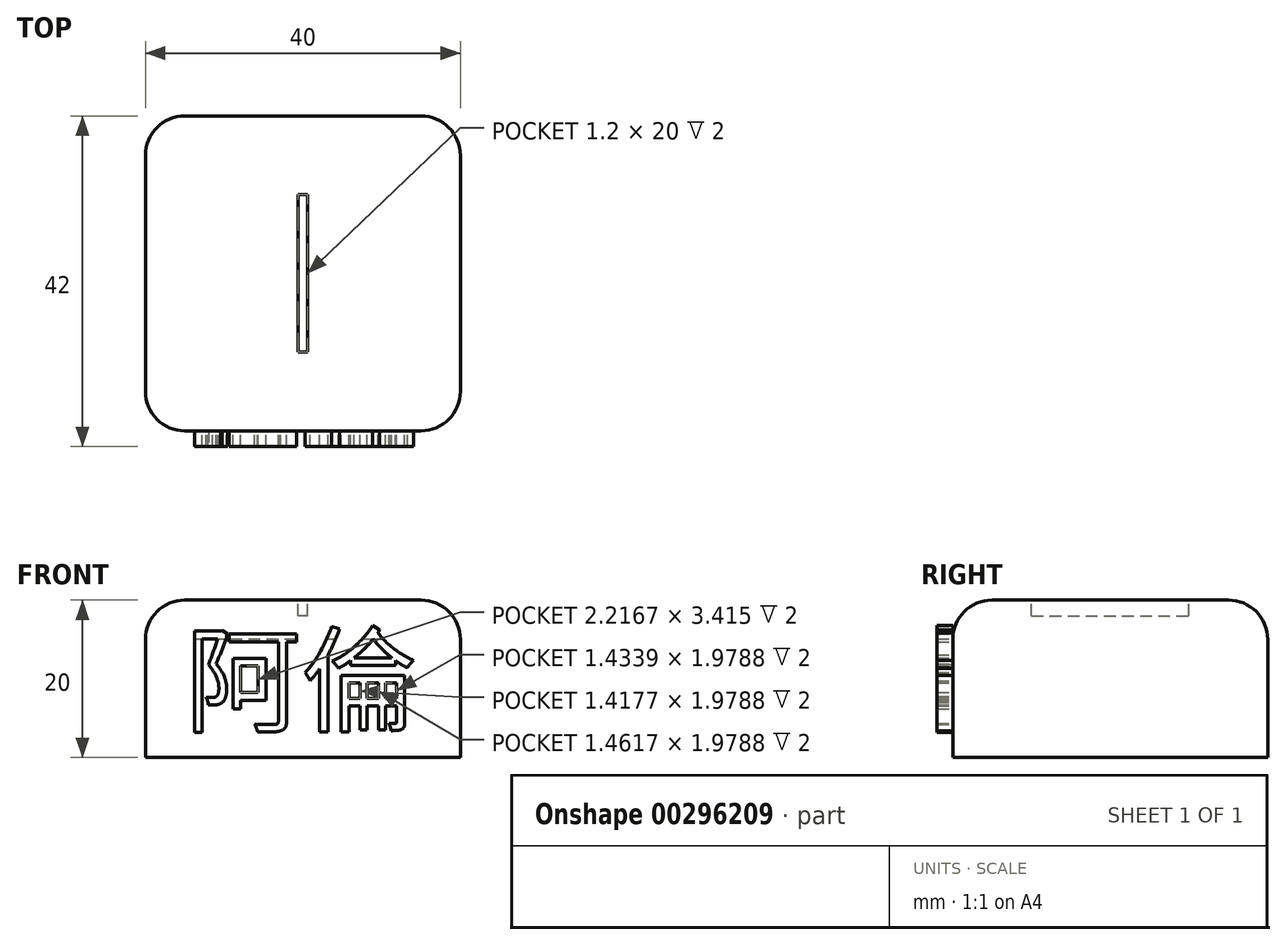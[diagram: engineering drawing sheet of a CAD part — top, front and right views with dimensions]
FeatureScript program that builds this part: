
annotation { "Feature Type Name" : "Feature", "Feature Type Description" : "" }
export const myFeature = defineFeature(function(context is Context, id is Id, definition is map)
    precondition{}
    {
        {
            var Q0;
            Q0=qCreatedBy(makeId("Top.planeOp"),FACE);
            var sketch = newSketch(context, id + "F0", { "sketchPlane" : qUnion([Q0])});
            skLineSegment(sketch, "E0.bottom", {"start": v(20, -20) * mm, "end": v(-20, -20) * mm});
            skLineSegment(sketch, "E0.top", {"start": v(20, 20) * mm, "end": v(-20, 20) * mm});
            skLineSegment(sketch, "E0.left", {"start": v(20, -20) * mm, "end": v(20, 20) * mm});
            skLineSegment(sketch, "E0.right", {"start": v(-20, -20) * mm, "end": v(-20, 20) * mm});
            skPoint(sketch, "E0.middle", {"position": v(0, 0) * mm});
            skLineSegment(sketch, "E1.bottom", {"start": v(0.6, -10) * mm, "end": v(-0.6, -10) * mm});
            skLineSegment(sketch, "E1.top", {"start": v(0.6, 10) * mm, "end": v(-0.6, 10) * mm});
            skLineSegment(sketch, "E1.left", {"start": v(0.6, -10) * mm, "end": v(0.6, 10) * mm});
            skLineSegment(sketch, "E1.right", {"start": v(-0.6, -10) * mm, "end": v(-0.6, 10) * mm});
            skSolve(sketch);
        }
        {
            var Q0;
            Q0=makeQuery(id+"F0.imprint","IMPRINT",FACE,{"disambiguationData":[TD([[makeQuery(id+"F0.imprint","IMPRINT",EDGE,{"derivedFrom":sQuery(id+"F0.wireOp",EDGE,"E0.bottom")}),-1.0]])]});
            var Q1;
            Q1=makeQuery(id+"F0.imprint","IMPRINT",FACE,{"disambiguationData":[TD([[makeQuery(id+"F0.imprint","IMPRINT",EDGE,{"derivedFrom":sQuery(id+"F0.wireOp",EDGE,"E1.bottom")}),-1.0]])]});
            extrude(context, id + "F1", {"entities" : qUnion([Q0, Q1]), "oppositeDirection" : true, "depth" : 20 * mm});
        }
        {
            var Q0;
            Q0=makeQuery(id+"F0.imprint","IMPRINT",FACE,{"disambiguationData":[TD([[makeQuery(id+"F0.imprint","IMPRINT",EDGE,{"derivedFrom":sQuery(id+"F0.wireOp",EDGE,"E1.bottom")}),-1.0]])]});
            extrude(context, id + "F2", {"entities" : qUnion([Q0]), "operationType" : NewBodyOperationType.REMOVE, "oppositeDirection" : true, "depth" : 2 * mm});
        }
        {
            var Q0;
            Q0=makeQuery(id+"F2.boolean.opBoolean","COPY",EDGE,{"derivedFrom":makeQuery(id+"F2.opExtrude","CAP_EDGE",EDGE,{"disambiguationData":[OSD([sQuery(id+"F0.wireOp",EDGE,"E1.left")])],"isStart":true})});
            var Q1;
            Q1=makeQuery(id+"F2.boolean.opBoolean","COPY",EDGE,{"derivedFrom":makeQuery(id+"F2.opExtrude","CAP_EDGE",EDGE,{"disambiguationData":[OSD([sQuery(id+"F0.wireOp",EDGE,"E1.right")])],"isStart":true})});
            var Q2;
            Q2=makeQuery(id+"F1.opExtrude","SWEPT_EDGE",EDGE,{"disambiguationData":[OSD([sQuery(id+"F0.wireOp",EDGE,"E0.bottom"),sQuery(id+"F0.wireOp",EDGE,"E0.left")])]});
            var Q3;
            Q3=makeQuery(id+"F1.opExtrude","SWEPT_EDGE",EDGE,{"disambiguationData":[OSD([sQuery(id+"F0.wireOp",EDGE,"E0.top"),sQuery(id+"F0.wireOp",EDGE,"E0.left")])]});
            var Q4;
            Q4=makeQuery(id+"F1.opExtrude","CAP_EDGE",EDGE,{"disambiguationData":[OSD([sQuery(id+"F0.wireOp",EDGE,"E0.left")])],"isStart":true});
            var Q5;
            Q5=makeQuery(id+"F1.opExtrude","SWEPT_EDGE",EDGE,{"disambiguationData":[OSD([sQuery(id+"F0.wireOp",EDGE,"E0.bottom"),sQuery(id+"F0.wireOp",EDGE,"E0.right")])]});
            var Q6;
            Q6=makeQuery(id+"F1.opExtrude","SWEPT_EDGE",EDGE,{"disambiguationData":[OSD([sQuery(id+"F0.wireOp",EDGE,"E0.top"),sQuery(id+"F0.wireOp",EDGE,"E0.right")])]});
            var Q7;
            Q7=makeQuery(id+"F1.opExtrude","CAP_EDGE",EDGE,{"disambiguationData":[OSD([sQuery(id+"F0.wireOp",EDGE,"E0.top")])],"isStart":true});
            var Q8;
            Q8=makeQuery(id+"F1.opExtrude","CAP_EDGE",EDGE,{"disambiguationData":[OSD([sQuery(id+"F0.wireOp",EDGE,"E0.right")])],"isStart":true});
            var Q9;
            Q9=makeQuery(id+"F1.opExtrude","CAP_EDGE",EDGE,{"disambiguationData":[OSD([sQuery(id+"F0.wireOp",EDGE,"E0.bottom")])],"isStart":true});
            fillet(context, id + "F3", {"entities" : qUnion([Q0, Q1, Q2, Q3, Q4, Q5, Q6, Q7, Q8, Q9]), "radius" : 5 * mm, "tangentPropagation" : true, "allowEdgeOverflow" : false});
        }
        {
            var Q0;
            Q0=makeQuery(id+"F1.opExtrude","SWEPT_FACE",FACE,{"disambiguationData":[OSD([sQuery(id+"F0.wireOp",EDGE,"E0.bottom")])]});
            var sketch = newSketch(context, id + "F4", { "sketchPlane" : qUnion([Q0])});
            skText(sketch, "E2", { "text": "阿倫", "fontName": "NotoSansCJKtc-Regular.otf"});
            const initialGuessF4  = {"E2": [-0.015, -0.01564, 1, 0, 0.01064]};
            skSetInitialGuess(sketch, initialGuessF4);
            skSolve(sketch);
        }
        {
            var Q0;
            Q0=makeQuery(id+"F4.imprint","IMPRINT",FACE,{"disambiguationData":[TD([[makeQuery(id+"F4.imprint","IMPRINT",EDGE,{"derivedFrom":sQuery(id+"F4.wireOp",EDGE,"E2.sketch_text.stroke-18")}),1.0]])]});
            var Q1;
            Q1=makeQuery(id+"F4.imprint","IMPRINT",FACE,{"disambiguationData":[TD([[makeQuery(id+"F4.imprint","IMPRINT",EDGE,{"derivedFrom":sQuery(id+"F4.wireOp",EDGE,"E2.sketch_text.stroke-0")}),1.0]])]});
            var Q2;
            {var subQ1=sQuery(id+"F4.wireOp",EDGE,"E2.sketch_text.stroke-7");Q2=makeQuery(id+"F4.imprint","IMPRINT",FACE,{"disambiguationData":[TD([[makeQuery(id+"F4.imprint","IMPRINT",EDGE,{"derivedFrom":subQ1}),1.0]])]});}
            var Q3;
            {var subQ0=sQuery(id+"F4.wireOp",EDGE,"E2.sketch_text.stroke-3");Q3=makeQuery(id+"F4.imprint","IMPRINT",FACE,{"disambiguationData":[TD([[makeQuery(id+"F4.imprint","IMPRINT",EDGE,{"derivedFrom":subQ0}),1.0]])]});}
            var Q4;
            {var subQ0=sQuery(id+"F4.wireOp",EDGE,"E2.sketch_text.stroke-28");Q4=makeQuery(id+"F4.imprint","IMPRINT",FACE,{"disambiguationData":[TD([[makeQuery(id+"F4.imprint","IMPRINT",EDGE,{"derivedFrom":subQ0}),1.0]])]});}
            var Q5;
            {var subQ1=sQuery(id+"F4.wireOp",EDGE,"E2.sketch_text.stroke-30");Q5=makeQuery(id+"F4.imprint","IMPRINT",FACE,{"disambiguationData":[TD([[makeQuery(id+"F4.imprint","IMPRINT",EDGE,{"derivedFrom":subQ1}),1.0]])]});}
            var Q6;
            {var subQ0=sQuery(id+"F4.wireOp",EDGE,"E2.sketch_text.stroke-41");Q6=makeQuery(id+"F4.imprint","IMPRINT",FACE,{"disambiguationData":[TD([[makeQuery(id+"F4.imprint","IMPRINT",EDGE,{"derivedFrom":subQ0}),1.0]])]});}
            var Q7;
            {var subQ0=sQuery(id+"F4.wireOp",EDGE,"E2.sketch_text.stroke-47");Q7=makeQuery(id+"F4.imprint","IMPRINT",FACE,{"disambiguationData":[TD([[makeQuery(id+"F4.imprint","IMPRINT",EDGE,{"derivedFrom":subQ0}),1.0]])]});}
            var Q8;
            {var subQ0=sQuery(id+"F4.wireOp",EDGE,"E2.sketch_text.stroke-92");Q8=makeQuery(id+"F4.imprint","IMPRINT",FACE,{"disambiguationData":[TD([[makeQuery(id+"F4.imprint","IMPRINT",EDGE,{"derivedFrom":subQ0}),1.0]])]});}
            var Q9;
            {var subQ11=sQuery(id+"F4.wireOp",EDGE,"E2.sketch_text.stroke-82");Q9=makeQuery(id+"F4.imprint","IMPRINT",FACE,{"disambiguationData":[TD([[makeQuery(id+"F4.imprint","IMPRINT",EDGE,{"derivedFrom":subQ11}),1.0]])]});}
            var Q10;
            Q10=makeQuery(id+"F4.imprint","IMPRINT",FACE,{"disambiguationData":[TD([[makeQuery(id+"F4.imprint","IMPRINT",EDGE,{"derivedFrom":sQuery(id+"F4.wireOp",EDGE,"E2.sketch_text.stroke-48")}),1.0]])]});
            extrude(context, id + "F5", {"entities" : qUnion([Q0, Q1, Q2, Q3, Q4, Q5, Q6, Q7, Q8, Q9, Q10]), "operationType" : NewBodyOperationType.ADD, "depth" : 2 * mm});
        }
    });
